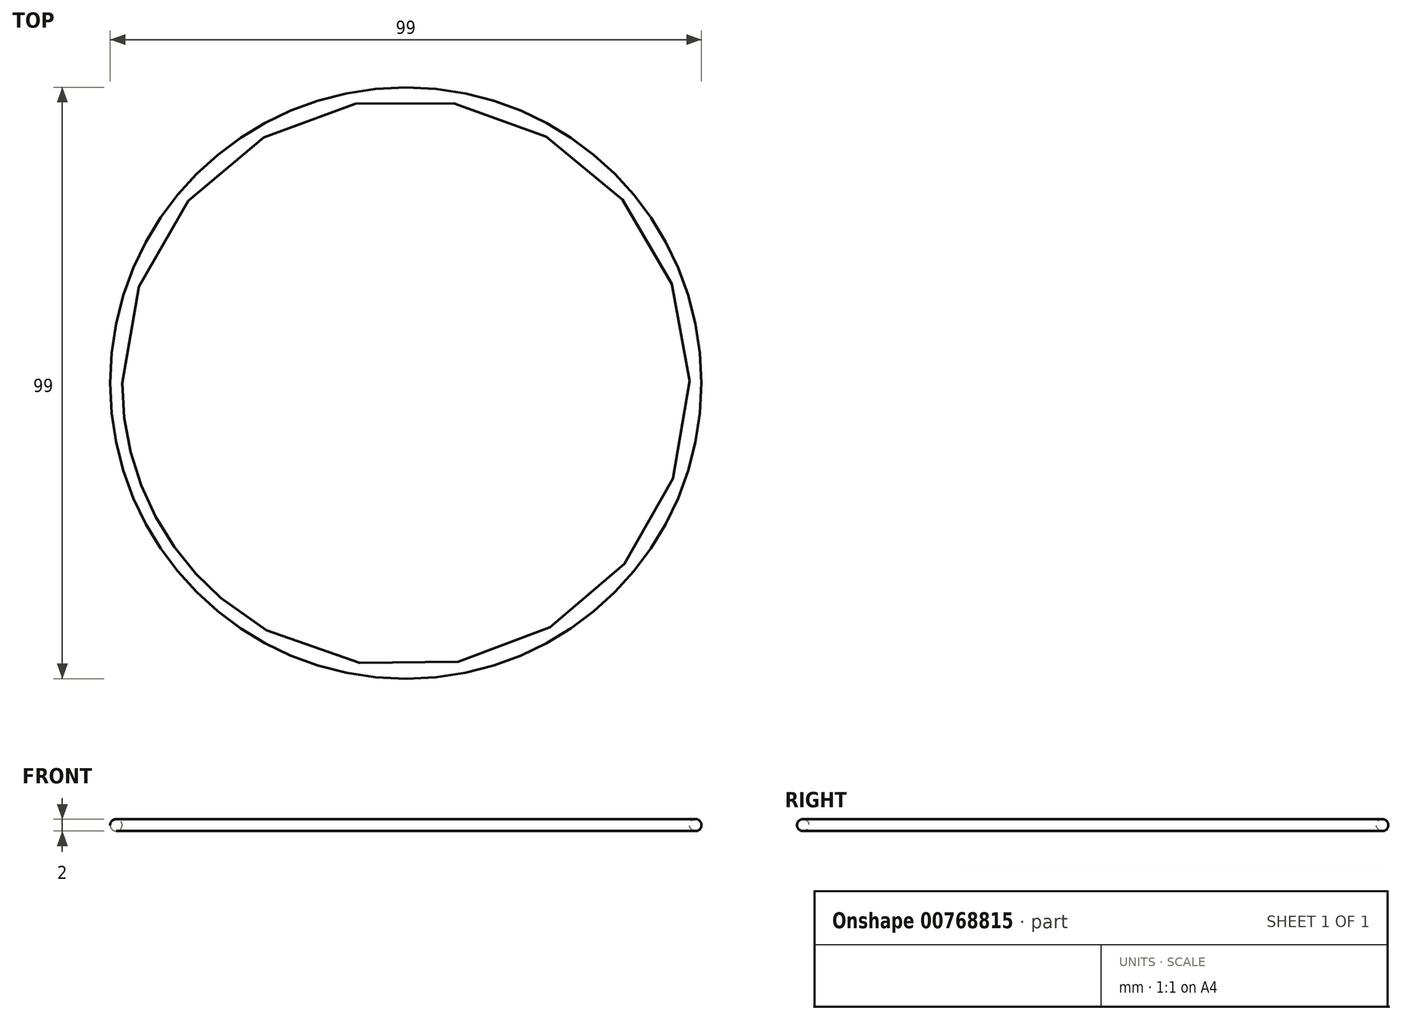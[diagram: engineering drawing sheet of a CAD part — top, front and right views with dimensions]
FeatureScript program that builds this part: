
annotation { "Feature Type Name" : "Feature", "Feature Type Description" : "" }
export const myFeature = defineFeature(function(context is Context, id is Id, definition is map)
    precondition{}
    {
        {
            var Q0;
            Q0=qCreatedBy(makeId("Front.planeOp"),FACE);
            var sketch = newSketch(context, id + "F0", { "sketchPlane" : qUnion([Q0])});
            skLineSegment(sketch, "E0", {"start": v(0, 0) * mm, "end": v(48.5, 0) * mm, "construction": true});
            skCircle(sketch, "E1", {"center": v(48.5, 0) * mm, "radius": 1 * mm});
            skLineSegment(sketch, "E2", {"start": v(0, 0) * mm, "end": v(0, 67.97) * mm});
            skSolve(sketch);
        }
        {
            var Q0;
            Q0=makeQuery(id+"F0.imprint","IMPRINT",FACE,{"disambiguationData":[TD([[makeQuery(id+"F0.imprint","IMPRINT",EDGE,{"derivedFrom":sQuery(id+"F0.wireOp",EDGE,"E1")}),1.0]])]});
            var Q1;
            Q1=sQuery(id+"F0.wireOp",EDGE,"E2");
            revolve(context, id + "F1", {"surfaceOperationType" : NewSurfaceOperationType.NEW, "entities" : qUnion([Q0]), "axis" : qUnion([Q1]), "revolveType" : RevolveType.FULL});
        }
    });
